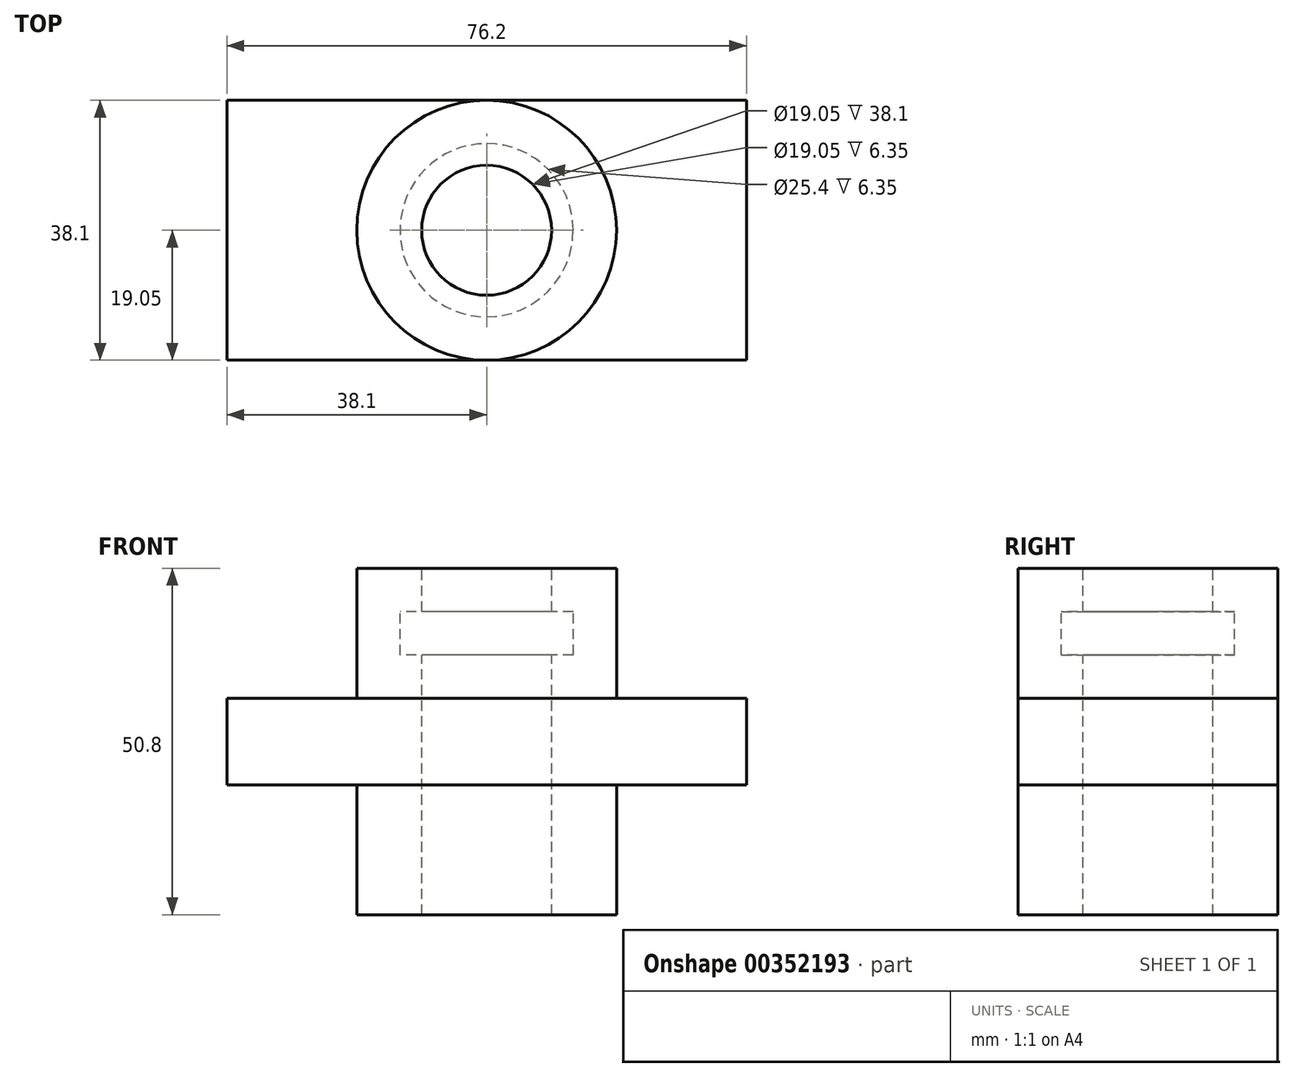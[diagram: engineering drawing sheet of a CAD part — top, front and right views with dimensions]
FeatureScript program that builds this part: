
annotation { "Feature Type Name" : "Feature", "Feature Type Description" : "" }
export const myFeature = defineFeature(function(context is Context, id is Id, definition is map)
    precondition{}
    {
        {
            var Q0;
            Q0=qCreatedBy(makeId("Top.planeOp"),FACE);
            var sketch = newSketch(context, id + "F0", { "sketchPlane" : qUnion([Q0])});
            skLineSegment(sketch, "E0", {"start": v(0, 0) * mm, "end": v(76.2, 0) * mm});
            skLineSegment(sketch, "E1", {"start": v(76.2, 0) * mm, "end": v(76.2, 38.1) * mm});
            skLineSegment(sketch, "E2", {"start": v(76.2, 38.1) * mm, "end": v(0, 38.1) * mm});
            skLineSegment(sketch, "E3", {"start": v(0, 38.1) * mm, "end": v(0, 0) * mm});
            skSolve(sketch);
        }
        {
            var Q0;
            Q0 = qSketchRegion(id + "F0", true);
            extrude(context, id + "F1", {"entities" : qUnion([Q0]), "depth" : 12.7 * mm});
        }
        {
            var Q0;
            Q0=makeQuery(id+"F1.opExtrude","CAP_FACE",FACE,{"disambiguationData":[OSD([sQuery(id+"F0.wireOp",EDGE,"E0"),sQuery(id+"F0.wireOp",EDGE,"E1"),sQuery(id+"F0.wireOp",EDGE,"E2"),sQuery(id+"F0.wireOp",EDGE,"E3")])],"isStart":false});
            var sketch = newSketch(context, id + "F2", { "sketchPlane" : qUnion([Q0])});
            skCircle(sketch, "E4", {"center": v(38.1, 19.05) * mm, "radius": 19.05 * mm});
            skSolve(sketch);
        }
        {
            var Q0;
            Q0 = qSketchRegion(id + "F2", true);
            extrude(context, id + "F3", {"entities" : qUnion([Q0]), "operationType" : NewBodyOperationType.ADD, "depth" : 19.05 * mm});
        }
        {
            var Q0;
            Q0=makeQuery(id+"F1.opExtrude","CAP_FACE",FACE,{"disambiguationData":[OSD([sQuery(id+"F0.wireOp",EDGE,"E0"),sQuery(id+"F0.wireOp",EDGE,"E1"),sQuery(id+"F0.wireOp",EDGE,"E2"),sQuery(id+"F0.wireOp",EDGE,"E3")])],"isStart":true});
            var sketch = newSketch(context, id + "F4", { "sketchPlane" : qUnion([Q0])});
            skCircle(sketch, "E5", {"center": v(38.1, -19.05) * mm, "radius": 19.05 * mm});
            skSolve(sketch);
        }
        {
            var Q0;
            Q0 = qSketchRegion(id + "F4", true);
            extrude(context, id + "F5", {"entities" : qUnion([Q0]), "operationType" : NewBodyOperationType.ADD, "depth" : 19.05 * mm});
        }
        {
            var Q0;
            Q0=makeQuery(id+"F3.opExtrude","CAP_FACE",FACE,{"disambiguationData":[OSD([sQuery(id+"F2.wireOp",EDGE,"E4")])],"isStart":false});
            var sketch = newSketch(context, id + "F6", { "sketchPlane" : qUnion([Q0])});
            skCircle(sketch, "E6", {"center": v(38.1, 19.05) * mm, "radius": 9.53 * mm});
            skSolve(sketch);
        }
        {
            var Q0;
            Q0 = qSketchRegion(id + "F6", true);
            extrude(context, id + "F7", {"entities" : qUnion([Q0]), "operationType" : NewBodyOperationType.REMOVE, "endBound" : BoundingType.THROUGH_ALL, "oppositeDirection" : true, "depth" : 25.4 * mm});
        }
        {
            var Q0;
            Q0=makeQuery(id+"F3.opExtrude","CAP_FACE",FACE,{"disambiguationData":[OSD([sQuery(id+"F2.wireOp",EDGE,"E4")])],"isStart":false});
            var sketch = newSketch(context, id + "F8", { "sketchPlane" : qUnion([Q0])});
            skCircle(sketch, "E7", {"center": v(38.1, 19.05) * mm, "radius": 12.7 * mm});
            skSolve(sketch);
        }
        {
            var Q0;
            Q0 = qSketchRegion(id + "F8", true);
            extrude(context, id + "F9", {"entities" : qUnion([Q0]), "operationType" : NewBodyOperationType.REMOVE, "oppositeDirection" : true, "depth" : 12.7 * mm, "hasSecondDirection" : true, "secondDirectionOppositeDirection" : true, "secondDirectionDepth" : 6.35 * mm});
        }
    });
